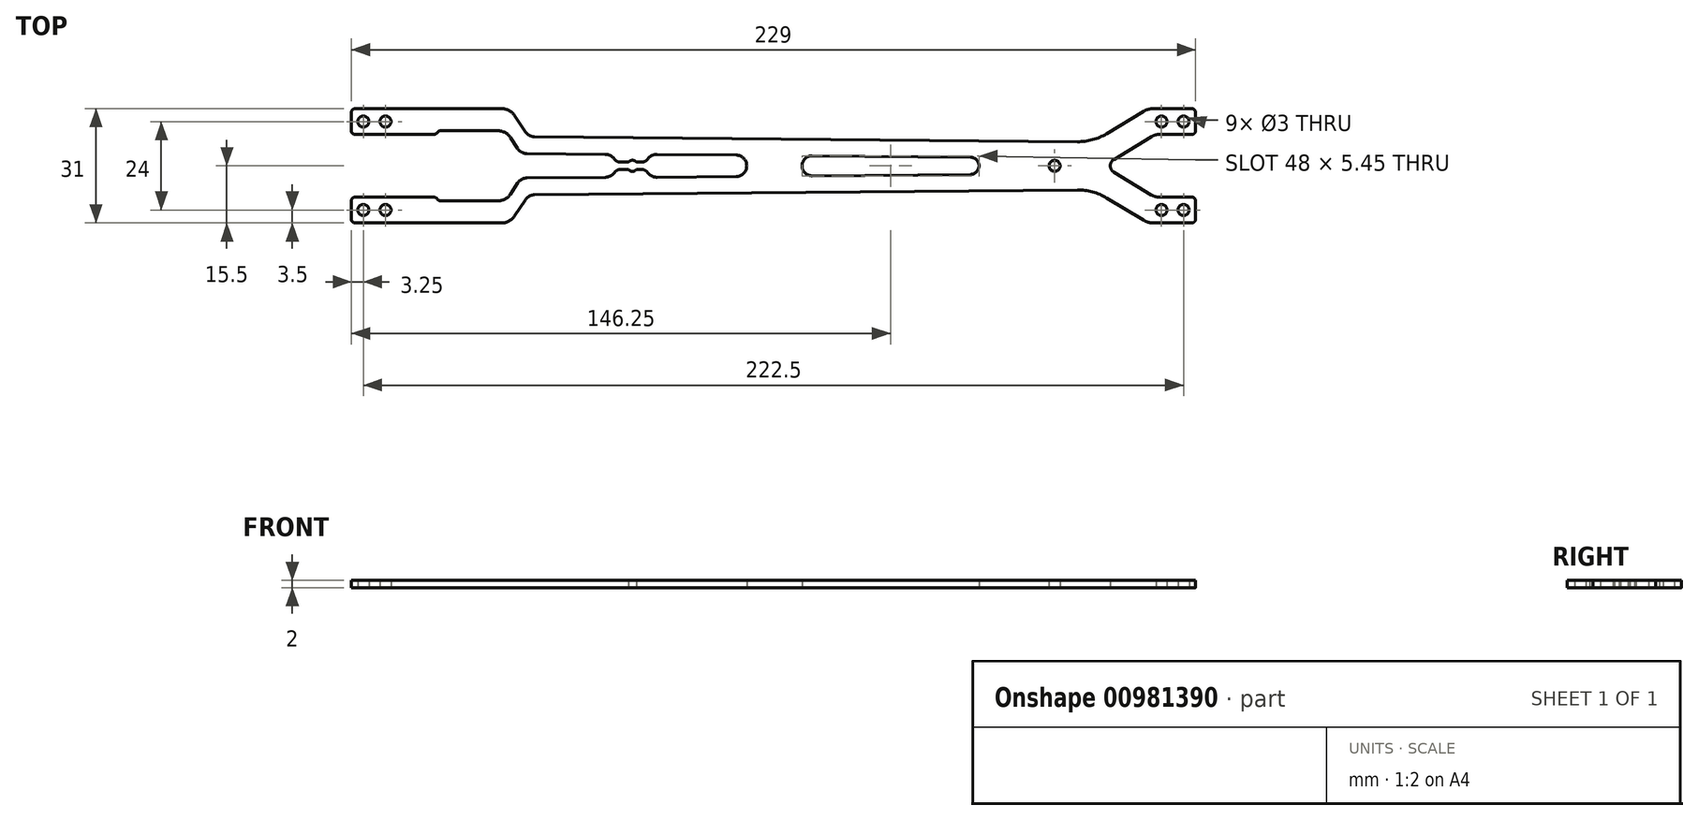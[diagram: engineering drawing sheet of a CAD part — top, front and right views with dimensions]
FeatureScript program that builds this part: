
annotation { "Feature Type Name" : "Feature", "Feature Type Description" : "" }
export const myFeature = defineFeature(function(context is Context, id is Id, definition is map)
    precondition{}
    {
        {
            var Q0;
            Q0=qCreatedBy(makeId("Top.planeOp"),FACE);
            var sketch = newSketch(context, id + "F0", { "sketchPlane" : qUnion([Q0])});
            skCircle(sketch, "E0", {"center": v(-91.58, -12) * mm, "radius": 1.5 * mm});
            skCircle(sketch, "E1", {"center": v(130.92, -12) * mm, "radius": 1.5 * mm});
            skCircle(sketch, "E2", {"center": v(-85.58, -12) * mm, "radius": 1.5 * mm});
            skCircle(sketch, "E3", {"center": v(-91.58, 12) * mm, "radius": 1.5 * mm});
            skCircle(sketch, "E4", {"center": v(-85.58, 12) * mm, "radius": 1.5 * mm});
            skCircle(sketch, "E5", {"center": v(130.92, 12) * mm, "radius": 1.5 * mm});
            skCircle(sketch, "E6", {"center": v(124.92, 12) * mm, "radius": 1.5 * mm});
            skCircle(sketch, "E7", {"center": v(124.92, -12) * mm, "radius": 1.5 * mm});
            skCircle(sketch, "E8", {"center": v(95.92, 0) * mm, "radius": 1.5 * mm});
            skArc(sketch, "E9", {"start": v(-17.46, 1) * mm, "mid": v(-18.58, 1.5) * mm, "end": v(-19.7, 1) * mm});
            skLineSegment(sketch, "E10", {"start": v(-94.83, -14.5) * mm, "end": v(-94.83, -9.5) * mm});
            skLineSegment(sketch, "E11", {"start": v(-93.83, -8.5) * mm, "end": v(-72.5, -8.5) * mm});
            skLineSegment(sketch, "E12", {"start": v(-93.83, -15.5) * mm, "end": v(-53.96, -15.5) * mm});
            skLineSegment(sketch, "E13", {"start": v(122.61, -15.5) * mm, "end": v(133.17, -15.5) * mm});
            skLineSegment(sketch, "E14", {"start": v(134.17, -14.5) * mm, "end": v(134.17, -9.5) * mm});
            skLineSegment(sketch, "E15", {"start": v(133.17, -8.5) * mm, "end": v(124.29, -8.5) * mm});
            skLineSegment(sketch, "E16", {"start": v(122.21, -7.92) * mm, "end": v(111.99, -1.7) * mm});
            skLineSegment(sketch, "E17.0", {"start": v(120.02, -14.77) * mm, "end": v(110.04, -8.72) * mm});
            skLineSegment(sketch, "E18", {"start": v(102.12, -6.54) * mm, "end": v(-45.15, -7.88) * mm});
            skLineSegment(sketch, "E19", {"start": v(-50.64, -13.72) * mm, "end": v(-47.62, -9.21) * mm});
            skLineSegment(sketch, "E20", {"start": v(-47.22, -3.3) * mm, "end": v(-25.96, -3.1) * mm});
            skLineSegment(sketch, "E21", {"start": v(-51.65, -7.67) * mm, "end": v(-49.7, -4.67) * mm});
            skLineSegment(sketch, "E22.MirrorCS", {"start": v(122.21, 7.92) * mm, "end": v(111.99, 1.7) * mm});
            skLineSegment(sketch, "E23.MirrorCS", {"start": v(133.17, 8.5) * mm, "end": v(124.29, 8.5) * mm});
            skLineSegment(sketch, "E24.MirrorCS", {"start": v(-93.83, 15.5) * mm, "end": v(-53.96, 15.5) * mm});
            skLineSegment(sketch, "E25.MirrorCS", {"start": v(134.17, 14.5) * mm, "end": v(134.17, 9.5) * mm});
            skLineSegment(sketch, "E26.MirrorCS", {"start": v(120.02, 14.77) * mm, "end": v(110.04, 8.72) * mm});
            skLineSegment(sketch, "E27.MirrorCS", {"start": v(122.61, 15.5) * mm, "end": v(133.17, 15.5) * mm});
            skLineSegment(sketch, "E28.MirrorCS", {"start": v(102.12, 6.54) * mm, "end": v(-45.15, 7.88) * mm});
            skLineSegment(sketch, "E29", {"start": v(-47.62, 9.21) * mm, "end": v(-50.64, 13.72) * mm});
            skLineSegment(sketch, "E30", {"start": v(-94.83, 14.5) * mm, "end": v(-94.83, 9.5) * mm});
            skLineSegment(sketch, "E31", {"start": v(-11.94, -3.1) * mm, "end": v(9.54, -2.91) * mm});
            skLineSegment(sketch, "E32.MirrorCS", {"start": v(-11.94, 3.1) * mm, "end": v(9.54, 2.91) * mm});
            skArc(sketch, "E33", {"start": v(-11.94, 3.1) * mm, "mid": v(-13.37, 2.78) * mm, "end": v(-14.49, 1.83) * mm});
            skArc(sketch, "E34", {"start": v(73.11, -2.33) * mm, "mid": v(75.42, 0) * mm, "end": v(73.11, 2.33) * mm});
            skLineSegment(sketch, "E35.trimOffspring", {"start": v(30.17, -2.72) * mm, "end": v(73.11, -2.33) * mm});
            skLineSegment(sketch, "E36.trimOffspring", {"start": v(30.17, 2.72) * mm, "end": v(73.11, 2.33) * mm});
            skArc(sketch, "E37", {"start": v(9.54, -2.91) * mm, "mid": v(12.42, 0) * mm, "end": v(9.54, 2.91) * mm});
            skArc(sketch, "E38", {"start": v(30.17, 2.72) * mm, "mid": v(27.42, 0) * mm, "end": v(30.17, -2.72) * mm});
            skLineSegment(sketch, "E39", {"start": v(-70.67, -9.5) * mm, "end": v(-55, -9.5) * mm});
            skLineSegment(sketch, "E40", {"start": v(-49.7, -4.67) * mm, "end": v(-51.65, -7.67) * mm});
            skLineSegment(sketch, "E41.MirrorCS", {"start": v(-70.67, 9.5) * mm, "end": v(-55, 9.5) * mm});
            skLineSegment(sketch, "E42", {"start": v(-71.37, -9.2) * mm, "end": v(-71.79, -8.8) * mm});
            skLineSegment(sketch, "E43.MirrorCS", {"start": v(-71.37, 9.2) * mm, "end": v(-71.79, 8.8) * mm});
            skLineSegment(sketch, "E44.MirrorCS", {"start": v(-93.83, 8.5) * mm, "end": v(-72.5, 8.5) * mm});
            skArc(sketch, "E45.filletArc", {"start": v(-71.37, -9.2) * mm, "mid": v(-71.05, -9.42) * mm, "end": v(-70.67, -9.5) * mm});
            skArc(sketch, "E46.filletArc", {"start": v(-71.79, -8.8) * mm, "mid": v(-72.11, -8.58) * mm, "end": v(-72.5, -8.5) * mm});
            skArc(sketch, "E47.filletArc", {"start": v(-70.67, 9.5) * mm, "mid": v(-71.05, 9.42) * mm, "end": v(-71.37, 9.2) * mm});
            skArc(sketch, "E48.filletArc", {"start": v(-72.5, 8.5) * mm, "mid": v(-72.11, 8.58) * mm, "end": v(-71.79, 8.8) * mm});
            skArc(sketch, "E49.filletArc", {"start": v(-55, -9.5) * mm, "mid": v(-53.1, -9.01) * mm, "end": v(-51.65, -7.67) * mm});
            skArc(sketch, "E50.filletArc", {"start": v(-51.65, 7.67) * mm, "mid": v(-53.1, 9.01) * mm, "end": v(-55, 9.5) * mm});
            skArc(sketch, "E51.filletArc", {"start": v(-47.22, -3.3) * mm, "mid": v(-48.63, -3.67) * mm, "end": v(-49.7, -4.67) * mm});
            skArc(sketch, "E52.filletArc", {"start": v(-47.62, 9.21) * mm, "mid": v(-46.55, 8.24) * mm, "end": v(-45.15, 7.88) * mm});
            skArc(sketch, "E53.filletArc", {"start": v(-45.15, -7.88) * mm, "mid": v(-46.55, -8.24) * mm, "end": v(-47.62, -9.21) * mm});
            skArc(sketch, "E54.filletArc", {"start": v(-50.64, 13.72) * mm, "mid": v(-52.08, 15.03) * mm, "end": v(-53.96, 15.5) * mm});
            skArc(sketch, "E55.filletArc", {"start": v(-53.96, -15.5) * mm, "mid": v(-52.08, -15.03) * mm, "end": v(-50.64, -13.72) * mm});
            skArc(sketch, "E56.filletArc", {"start": v(-94.83, -14.5) * mm, "mid": v(-94.54, -15.2) * mm, "end": v(-93.83, -15.5) * mm});
            skArc(sketch, "E57.filletArc", {"start": v(-93.83, -8.5) * mm, "mid": v(-94.54, -8.8) * mm, "end": v(-94.83, -9.5) * mm});
            skArc(sketch, "E58.filletArc", {"start": v(-94.83, 9.5) * mm, "mid": v(-94.54, 8.8) * mm, "end": v(-93.83, 8.5) * mm});
            skArc(sketch, "E59.filletArc", {"start": v(-93.83, 15.5) * mm, "mid": v(-94.54, 15.2) * mm, "end": v(-94.83, 14.5) * mm});
            skPoint(sketch, "E60.visualSharp", {"position": v(134.17, 15.5) * mm});
            skArc(sketch, "E60.filletArc", {"start": v(134.17, 14.5) * mm, "mid": v(133.88, 15.2) * mm, "end": v(133.17, 15.5) * mm});
            skPoint(sketch, "E61.visualSharp", {"position": v(134.17, 8.5) * mm});
            skArc(sketch, "E61.filletArc", {"start": v(133.17, 8.5) * mm, "mid": v(133.88, 8.8) * mm, "end": v(134.17, 9.5) * mm});
            skPoint(sketch, "E62.visualSharp", {"position": v(134.17, -8.5) * mm});
            skArc(sketch, "E62.filletArc", {"start": v(134.17, -9.5) * mm, "mid": v(133.88, -8.8) * mm, "end": v(133.17, -8.5) * mm});
            skPoint(sketch, "E63.visualSharp", {"position": v(134.17, -15.5) * mm});
            skArc(sketch, "E63.filletArc", {"start": v(133.17, -15.5) * mm, "mid": v(133.88, -15.2) * mm, "end": v(134.17, -14.5) * mm});
            skPoint(sketch, "E64.visualSharp", {"position": v(123.17, 8.5) * mm});
            skArc(sketch, "E64.filletArc", {"start": v(124.29, 8.5) * mm, "mid": v(123.21, 8.35) * mm, "end": v(122.21, 7.92) * mm});
            skPoint(sketch, "E65.visualSharp", {"position": v(123.17, -8.5) * mm});
            skArc(sketch, "E65.filletArc", {"start": v(122.21, -7.92) * mm, "mid": v(123.21, -8.35) * mm, "end": v(124.29, -8.5) * mm});
            skPoint(sketch, "E66.visualSharp", {"position": v(121.21, 15.5) * mm});
            skArc(sketch, "E66.filletArc", {"start": v(122.61, 15.5) * mm, "mid": v(121.26, 15.32) * mm, "end": v(120.02, 14.77) * mm});
            skPoint(sketch, "E67.visualSharp", {"position": v(121.21, -15.5) * mm});
            skArc(sketch, "E67.filletArc", {"start": v(120.02, -14.77) * mm, "mid": v(121.26, -15.32) * mm, "end": v(122.61, -15.5) * mm});
            skPoint(sketch, "E68.visualSharp", {"position": v(106.39, -6.5) * mm});
            skArc(sketch, "E68.filletArc", {"start": v(110.04, -8.72) * mm, "mid": v(106.23, -7.07) * mm, "end": v(102.12, -6.54) * mm});
            skPoint(sketch, "E69.visualSharp", {"position": v(106.39, 6.5) * mm});
            skArc(sketch, "E69.filletArc", {"start": v(102.12, 6.54) * mm, "mid": v(106.23, 7.07) * mm, "end": v(110.04, 8.72) * mm});
            skPoint(sketch, "E70.visualSharp", {"position": v(109.17, 0) * mm});
            skArc(sketch, "E70.filletArc", {"start": v(111.99, 1.7) * mm, "mid": v(111.02, 0) * mm, "end": v(111.99, -1.7) * mm});
            skLineSegment(sketch, "E71.MirrorCS", {"start": v(-47.22, 3.3) * mm, "end": v(-25.96, 3.1) * mm});
            skArc(sketch, "E72.MirrorCS", {"start": v(-47.22, 3.3) * mm, "mid": v(-48.63, 3.67) * mm, "end": v(-49.7, 4.67) * mm});
            skLineSegment(sketch, "E73.MirrorCS", {"start": v(-51.65, 7.67) * mm, "end": v(-49.7, 4.67) * mm});
            skArc(sketch, "E74", {"start": v(-25.96, -3.1) * mm, "mid": v(-24.56, -2.76) * mm, "end": v(-23.47, -1.83) * mm});
            skLineSegment(sketch, "E75", {"start": v(-21.85, -1) * mm, "end": v(-19.7, -1) * mm});
            skLineSegment(sketch, "E76.MirrorCS", {"start": v(-21.85, 1) * mm, "end": v(-19.7, 1) * mm});
            skArc(sketch, "E77.trimOffspring", {"start": v(-23.47, 1.83) * mm, "mid": v(-24.56, 2.76) * mm, "end": v(-25.96, 3.1) * mm});
            skArc(sketch, "E78.trimOffspring", {"start": v(-14.49, -1.83) * mm, "mid": v(-13.37, -2.78) * mm, "end": v(-11.94, -3.1) * mm});
            skArc(sketch, "E79.trimOffspring", {"start": v(-19.7, -1) * mm, "mid": v(-18.58, -1.5) * mm, "end": v(-17.46, -1) * mm});
            skLineSegment(sketch, "E80.trimOffspring", {"start": v(-17.46, 1) * mm, "end": v(-16.1, 1) * mm});
            skLineSegment(sketch, "E81.trimOffspring", {"start": v(-17.46, -1) * mm, "end": v(-16.1, -1) * mm});
            skPoint(sketch, "E82.visualSharp", {"position": v(-23.04, 1) * mm});
            skArc(sketch, "E82.filletArc", {"start": v(-23.47, 1.83) * mm, "mid": v(-22.76, 1.22) * mm, "end": v(-21.85, 1) * mm});
            skPoint(sketch, "E83.visualSharp", {"position": v(-23.04, -1) * mm});
            skArc(sketch, "E83.filletArc", {"start": v(-21.85, -1) * mm, "mid": v(-22.76, -1.22) * mm, "end": v(-23.47, -1.83) * mm});
            skPoint(sketch, "E84.visualSharp", {"position": v(-14.91, 1) * mm});
            skArc(sketch, "E84.filletArc", {"start": v(-16.1, 1) * mm, "mid": v(-15.2, 1.22) * mm, "end": v(-14.49, 1.83) * mm});
            skPoint(sketch, "E85.visualSharp", {"position": v(-14.91, -1) * mm});
            skArc(sketch, "E85.filletArc", {"start": v(-14.49, -1.83) * mm, "mid": v(-15.2, -1.22) * mm, "end": v(-16.1, -1) * mm});
            skSolve(sketch);
        }
        {
            var Q0;
            Q0=makeQuery(id+"F0.imprint","IMPRINT",FACE,{"disambiguationData":[TD([[makeQuery(id+"F0.imprint","IMPRINT",EDGE,{"derivedFrom":sQuery(id+"F0.wireOp",EDGE,"E0")}),-1.0]])]});
            extrude(context, id + "F1", {"entities" : qUnion([Q0]), "depth" : 2 * mm, "offsetDistance" : 25 * mm});
        }
    });
